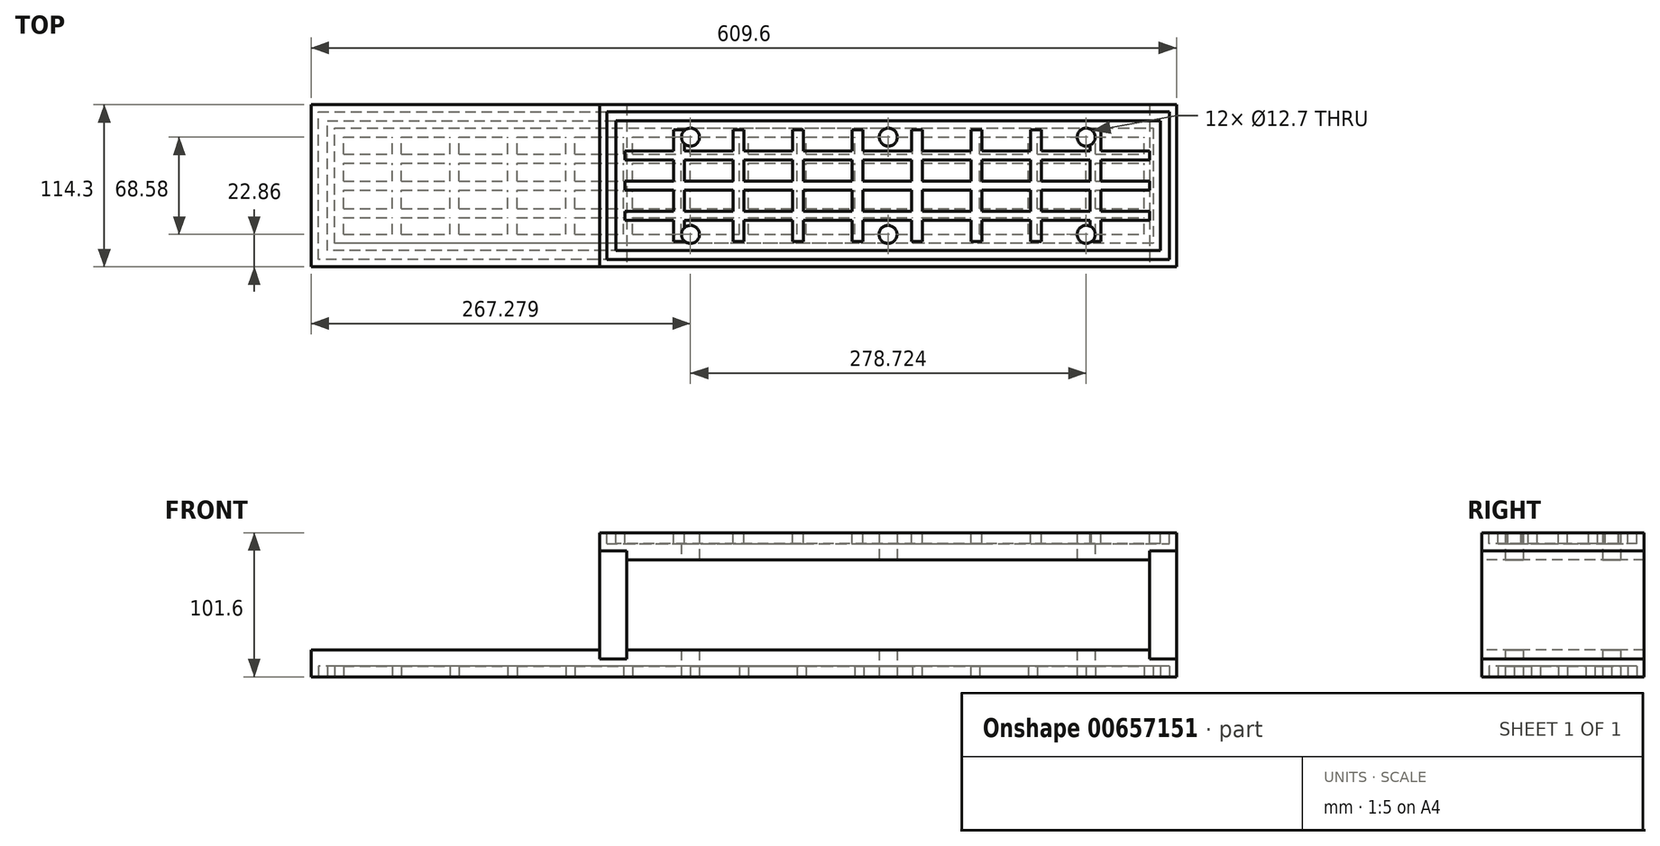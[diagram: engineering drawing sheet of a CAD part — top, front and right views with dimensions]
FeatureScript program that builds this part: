
annotation { "Feature Type Name" : "Feature", "Feature Type Description" : "" }
export const myFeature = defineFeature(function(context is Context, id is Id, definition is map)
    precondition{}
    {
        {
            var Q0;
            Q0=qCreatedBy(makeId("Front.planeOp"),FACE);
            var sketch = newSketch(context, id + "F0", { "sketchPlane" : qUnion([Q0])});
            skLineSegment(sketch, "E0.bottom", {"start": v(203.2, 50.8) * mm, "end": v(-203.2, 50.8) * mm});
            skLineSegment(sketch, "E0.top", {"start": v(203.2, -50.8) * mm, "end": v(-203.2, -50.8) * mm});
            skLineSegment(sketch, "E0.left", {"start": v(203.2, 50.8) * mm, "end": v(203.2, -50.8) * mm});
            skLineSegment(sketch, "E0.right", {"start": v(-203.2, 50.8) * mm, "end": v(-203.2, -38.1) * mm});
            skPoint(sketch, "E0.middle", {"position": v(0, 0) * mm});
            skLineSegment(sketch, "E1.0", {"start": v(184.15, 31.75) * mm, "end": v(-184.15, 31.75) * mm});
            skLineSegment(sketch, "E1.1", {"start": v(184.15, 31.75) * mm, "end": v(184.15, -31.75) * mm});
            skLineSegment(sketch, "E1.2", {"start": v(184.15, -31.75) * mm, "end": v(-184.15, -31.75) * mm});
            skLineSegment(sketch, "E1.3", {"start": v(-184.15, 31.75) * mm, "end": v(-184.15, -31.75) * mm});
            skLineSegment(sketch, "E2", {"start": v(-184.15, 31.75) * mm, "end": v(-184.15, 38.1) * mm});
            skLineSegment(sketch, "E3", {"start": v(-184.15, 38.1) * mm, "end": v(-203.2, 38.1) * mm});
            skLineSegment(sketch, "E4", {"start": v(-184.15, -31.75) * mm, "end": v(-184.15, -38.1) * mm});
            skLineSegment(sketch, "E5", {"start": v(-184.15, -38.1) * mm, "end": v(-203.2, -38.1) * mm});
            skLineSegment(sketch, "E6", {"start": v(184.15, -31.75) * mm, "end": v(184.15, -38.1) * mm});
            skLineSegment(sketch, "E7", {"start": v(184.15, -38.1) * mm, "end": v(203.2, -38.1) * mm});
            skLineSegment(sketch, "E8", {"start": v(184.15, 31.75) * mm, "end": v(184.15, 38.1) * mm});
            skLineSegment(sketch, "E9", {"start": v(184.15, 38.1) * mm, "end": v(203.2, 38.1) * mm});
            skLineSegment(sketch, "E10.bottom", {"start": v(-203.2, -50.8) * mm, "end": v(-406.4, -50.8) * mm});
            skLineSegment(sketch, "E10.top", {"start": v(-203.2, -31.75) * mm, "end": v(-406.4, -31.75) * mm});
            skLineSegment(sketch, "E10.left", {"start": v(-203.2, -38.1) * mm, "end": v(-203.2, -31.75) * mm});
            skLineSegment(sketch, "E10.right", {"start": v(-406.4, -50.8) * mm, "end": v(-406.4, -31.75) * mm});
            skSolve(sketch);
        }
        {
            var Q0;
            {var subQ2=sQuery(id+"F0.wireOp",EDGE,"E0.bottom");Q0=makeQuery(id+"F0.imprint","IMPRINT",FACE,{"disambiguationData":[TD([[makeQuery(id+"F0.imprint","IMPRINT",EDGE,{"derivedFrom":subQ2}),1.0]])]});}
            var Q1;
            {var subQ1=sQuery(id+"F0.wireOp",EDGE,"E0.top");Q1=makeQuery(id+"F0.imprint","IMPRINT",FACE,{"disambiguationData":[TD([[makeQuery(id+"F0.imprint","IMPRINT",EDGE,{"derivedFrom":subQ1}),-1.0]])]});}
            extrude(context, id + "F1", {"entities" : qUnion([Q0, Q1]), "oppositeDirection" : true, "depth" : 114.3 * mm, "offsetDistance" : 25.4 * mm});
        }
        {
            var Q0;
            Q0=makeQuery(id+"F0.imprint","IMPRINT",FACE,{"disambiguationData":[TD([[makeQuery(id+"F0.imprint","IMPRINT",EDGE,{"derivedFrom":sQuery(id+"F0.wireOp",EDGE,"E1.3")}),-1.0]])]});
            var Q1;
            Q1=makeQuery(id+"F0.imprint","IMPRINT",FACE,{"disambiguationData":[TD([[makeQuery(id+"F0.imprint","IMPRINT",EDGE,{"derivedFrom":sQuery(id+"F0.wireOp",EDGE,"E1.1")}),1.0]])]});
            extrude(context, id + "F2", {"entities" : qUnion([Q0, Q1]), "oppositeDirection" : true, "depth" : 114.3 * mm, "offsetDistance" : 25.4 * mm});
        }
        {
            var Q0;
            Q0=makeQuery(id+"F1.opExtrude","SWEPT_FACE",FACE,{"disambiguationData":[OSD([sQuery(id+"F0.wireOp",EDGE,"E0.top"),sQuery(id+"F0.wireOp",EDGE,"E10.bottom")])]});
            var sketch = newSketch(context, id + "F3", { "sketchPlane" : qUnion([Q0])});
            skLineSegment(sketch, "E11.0", {"start": v(198.12, -5.08) * mm, "end": v(-401.32, -5.08) * mm});
            skLineSegment(sketch, "E11.1", {"start": v(198.12, -109.22) * mm, "end": v(198.12, -5.08) * mm});
            skLineSegment(sketch, "E11.2", {"start": v(-401.32, -109.22) * mm, "end": v(198.12, -109.22) * mm});
            skLineSegment(sketch, "E11.3", {"start": v(-401.32, -5.08) * mm, "end": v(-401.32, -109.22) * mm});
            skLineSegment(sketch, "E12.0", {"start": v(191.77, -11.43) * mm, "end": v(-394.97, -11.43) * mm});
            skLineSegment(sketch, "E12.1", {"start": v(191.77, -102.87) * mm, "end": v(191.77, -11.43) * mm});
            skLineSegment(sketch, "E12.2", {"start": v(-394.97, -102.87) * mm, "end": v(191.77, -102.87) * mm});
            skLineSegment(sketch, "E12.3", {"start": v(-394.97, -11.43) * mm, "end": v(-394.97, -102.87) * mm});
            skLineSegment(sketch, "E13.bottom", {"start": v(-383.54, -22.86) * mm, "end": v(-349.23, -22.86) * mm});
            skLineSegment(sketch, "E13.top", {"start": v(-383.54, -34.8) * mm, "end": v(-349.23, -34.8) * mm});
            skLineSegment(sketch, "E13.left", {"start": v(-383.54, -22.86) * mm, "end": v(-383.54, -34.8) * mm});
            skLineSegment(sketch, "E13.right", {"start": v(-349.23, -22.86) * mm, "end": v(-349.23, -34.8) * mm});
            skLineSegment(sketch, "E14.bottom", {"start": v(-383.54, -41.15) * mm, "end": v(-349.23, -41.15) * mm});
            skLineSegment(sketch, "E14.top", {"start": v(-383.54, -53.99) * mm, "end": v(-349.23, -53.99) * mm});
            skLineSegment(sketch, "E14.left", {"start": v(-383.54, -41.15) * mm, "end": v(-383.54, -53.99) * mm});
            skLineSegment(sketch, "E14.right", {"start": v(-349.23, -41.15) * mm, "end": v(-349.23, -53.99) * mm});
            skLineSegment(sketch, "E15.bottom", {"start": v(-383.54, -79.53) * mm, "end": v(-349.23, -79.53) * mm});
            skLineSegment(sketch, "E15.top", {"start": v(-383.54, -91.44) * mm, "end": v(-349.23, -91.44) * mm});
            skLineSegment(sketch, "E15.left", {"start": v(-383.54, -79.53) * mm, "end": v(-383.54, -91.44) * mm});
            skLineSegment(sketch, "E15.right", {"start": v(-349.23, -79.53) * mm, "end": v(-349.23, -91.44) * mm});
            skLineSegment(sketch, "E16.1.0.0", {"start": v(-342.8, -34.8) * mm, "end": v(-308.5, -34.8) * mm});
            skLineSegment(sketch, "E16.1.0.1", {"start": v(-308.5, -79.53) * mm, "end": v(-308.5, -91.44) * mm});
            skLineSegment(sketch, "E16.1.0.2", {"start": v(-308.5, -41.15) * mm, "end": v(-308.5, -53.99) * mm});
            skLineSegment(sketch, "E16.1.0.3", {"start": v(-342.8, -22.86) * mm, "end": v(-308.5, -22.86) * mm});
            skLineSegment(sketch, "E16.1.0.4", {"start": v(-342.8, -41.15) * mm, "end": v(-308.5, -41.15) * mm});
            skLineSegment(sketch, "E16.1.0.5", {"start": v(-342.8, -22.86) * mm, "end": v(-342.8, -34.8) * mm});
            skLineSegment(sketch, "E16.1.0.6", {"start": v(-342.8, -91.44) * mm, "end": v(-308.5, -91.44) * mm});
            skLineSegment(sketch, "E16.1.0.7", {"start": v(-342.8, -79.53) * mm, "end": v(-342.8, -91.44) * mm});
            skLineSegment(sketch, "E16.1.0.8", {"start": v(-342.8, -79.53) * mm, "end": v(-308.5, -79.53) * mm});
            skLineSegment(sketch, "E16.1.0.9", {"start": v(-308.5, -22.86) * mm, "end": v(-308.5, -34.8) * mm});
            skLineSegment(sketch, "E16.1.0.10", {"start": v(-342.8, -41.15) * mm, "end": v(-342.8, -53.99) * mm});
            skLineSegment(sketch, "E16.1.0.11", {"start": v(-342.8, -53.99) * mm, "end": v(-308.5, -53.99) * mm});
            skLineSegment(sketch, "E16.2.0.0", {"start": v(-302.07, -34.8) * mm, "end": v(-267.76, -34.8) * mm});
            skLineSegment(sketch, "E16.2.0.1", {"start": v(-267.76, -79.53) * mm, "end": v(-267.76, -91.44) * mm});
            skLineSegment(sketch, "E16.2.0.2", {"start": v(-267.76, -41.15) * mm, "end": v(-267.76, -53.99) * mm});
            skLineSegment(sketch, "E16.2.0.3", {"start": v(-302.07, -22.86) * mm, "end": v(-267.76, -22.86) * mm});
            skLineSegment(sketch, "E16.2.0.4", {"start": v(-302.07, -41.15) * mm, "end": v(-267.76, -41.15) * mm});
            skLineSegment(sketch, "E16.2.0.5", {"start": v(-302.07, -22.86) * mm, "end": v(-302.07, -34.8) * mm});
            skLineSegment(sketch, "E16.2.0.6", {"start": v(-302.07, -91.44) * mm, "end": v(-267.76, -91.44) * mm});
            skLineSegment(sketch, "E16.2.0.7", {"start": v(-302.07, -79.53) * mm, "end": v(-302.07, -91.44) * mm});
            skLineSegment(sketch, "E16.2.0.8", {"start": v(-302.07, -79.53) * mm, "end": v(-267.76, -79.53) * mm});
            skLineSegment(sketch, "E16.2.0.9", {"start": v(-267.76, -22.86) * mm, "end": v(-267.76, -34.8) * mm});
            skLineSegment(sketch, "E16.2.0.10", {"start": v(-302.07, -41.15) * mm, "end": v(-302.07, -53.99) * mm});
            skLineSegment(sketch, "E16.2.0.11", {"start": v(-302.07, -53.99) * mm, "end": v(-267.76, -53.99) * mm});
            skLineSegment(sketch, "E16.3.0.0", {"start": v(-261.33, -34.8) * mm, "end": v(-227.03, -34.8) * mm});
            skLineSegment(sketch, "E16.3.0.1", {"start": v(-227.03, -79.53) * mm, "end": v(-227.03, -91.44) * mm});
            skLineSegment(sketch, "E16.3.0.2", {"start": v(-227.03, -41.15) * mm, "end": v(-227.03, -53.99) * mm});
            skLineSegment(sketch, "E16.3.0.3", {"start": v(-261.33, -22.86) * mm, "end": v(-227.03, -22.86) * mm});
            skLineSegment(sketch, "E16.3.0.4", {"start": v(-261.33, -41.15) * mm, "end": v(-227.03, -41.15) * mm});
            skLineSegment(sketch, "E16.3.0.5", {"start": v(-261.33, -22.86) * mm, "end": v(-261.33, -34.8) * mm});
            skLineSegment(sketch, "E16.3.0.6", {"start": v(-261.33, -91.44) * mm, "end": v(-227.03, -91.44) * mm});
            skLineSegment(sketch, "E16.3.0.7", {"start": v(-261.33, -79.53) * mm, "end": v(-261.33, -91.44) * mm});
            skLineSegment(sketch, "E16.3.0.8", {"start": v(-261.33, -79.53) * mm, "end": v(-227.03, -79.53) * mm});
            skLineSegment(sketch, "E16.3.0.9", {"start": v(-227.03, -22.86) * mm, "end": v(-227.03, -34.8) * mm});
            skLineSegment(sketch, "E16.3.0.10", {"start": v(-261.33, -41.15) * mm, "end": v(-261.33, -53.99) * mm});
            skLineSegment(sketch, "E16.3.0.11", {"start": v(-261.33, -53.99) * mm, "end": v(-227.03, -53.99) * mm});
            skLineSegment(sketch, "E16.4.0.0", {"start": v(-220.6, -34.8) * mm, "end": v(-186.29, -34.8) * mm});
            skLineSegment(sketch, "E16.4.0.1", {"start": v(-186.29, -79.53) * mm, "end": v(-186.29, -91.44) * mm});
            skLineSegment(sketch, "E16.4.0.2", {"start": v(-186.29, -41.15) * mm, "end": v(-186.29, -53.99) * mm});
            skLineSegment(sketch, "E16.4.0.3", {"start": v(-220.6, -22.86) * mm, "end": v(-186.29, -22.86) * mm});
            skLineSegment(sketch, "E16.4.0.4", {"start": v(-220.6, -41.15) * mm, "end": v(-186.29, -41.15) * mm});
            skLineSegment(sketch, "E16.4.0.5", {"start": v(-220.6, -22.86) * mm, "end": v(-220.6, -34.8) * mm});
            skLineSegment(sketch, "E16.4.0.6", {"start": v(-220.6, -91.44) * mm, "end": v(-186.29, -91.44) * mm});
            skLineSegment(sketch, "E16.4.0.7", {"start": v(-220.6, -79.53) * mm, "end": v(-220.6, -91.44) * mm});
            skLineSegment(sketch, "E16.4.0.8", {"start": v(-220.6, -79.53) * mm, "end": v(-186.29, -79.53) * mm});
            skLineSegment(sketch, "E16.4.0.9", {"start": v(-186.29, -22.86) * mm, "end": v(-186.29, -34.8) * mm});
            skLineSegment(sketch, "E16.4.0.10", {"start": v(-220.6, -41.15) * mm, "end": v(-220.6, -53.99) * mm});
            skLineSegment(sketch, "E16.4.0.11", {"start": v(-220.6, -53.99) * mm, "end": v(-186.29, -53.99) * mm});
            skLineSegment(sketch, "E16.5.0.0", {"start": v(-179.86, -34.8) * mm, "end": v(-145.55, -34.8) * mm});
            skLineSegment(sketch, "E16.5.0.1", {"start": v(-145.55, -79.53) * mm, "end": v(-145.55, -91.44) * mm});
            skLineSegment(sketch, "E16.5.0.2", {"start": v(-145.55, -41.15) * mm, "end": v(-145.55, -53.99) * mm});
            skLineSegment(sketch, "E16.5.0.3", {"start": v(-179.86, -22.86) * mm, "end": v(-145.55, -22.86) * mm});
            skLineSegment(sketch, "E16.5.0.4", {"start": v(-179.86, -41.15) * mm, "end": v(-145.55, -41.15) * mm});
            skLineSegment(sketch, "E16.5.0.5", {"start": v(-179.86, -22.86) * mm, "end": v(-179.86, -34.8) * mm});
            skLineSegment(sketch, "E16.5.0.6", {"start": v(-179.86, -91.44) * mm, "end": v(-145.55, -91.44) * mm});
            skLineSegment(sketch, "E16.5.0.7", {"start": v(-179.86, -79.53) * mm, "end": v(-179.86, -91.44) * mm});
            skLineSegment(sketch, "E16.5.0.8", {"start": v(-179.86, -79.53) * mm, "end": v(-145.55, -79.53) * mm});
            skLineSegment(sketch, "E16.5.0.9", {"start": v(-145.55, -22.86) * mm, "end": v(-145.55, -34.8) * mm});
            skLineSegment(sketch, "E16.5.0.10", {"start": v(-179.86, -41.15) * mm, "end": v(-179.86, -53.99) * mm});
            skLineSegment(sketch, "E16.5.0.11", {"start": v(-179.86, -53.99) * mm, "end": v(-145.55, -53.99) * mm});
            skLineSegment(sketch, "E16.6.0.0", {"start": v(-139.12, -34.8) * mm, "end": v(-104.82, -34.8) * mm});
            skLineSegment(sketch, "E16.6.0.1", {"start": v(-104.82, -79.53) * mm, "end": v(-104.82, -91.44) * mm});
            skLineSegment(sketch, "E16.6.0.2", {"start": v(-104.82, -41.15) * mm, "end": v(-104.82, -53.99) * mm});
            skLineSegment(sketch, "E16.6.0.3", {"start": v(-139.12, -22.86) * mm, "end": v(-104.82, -22.86) * mm});
            skLineSegment(sketch, "E16.6.0.4", {"start": v(-139.12, -41.15) * mm, "end": v(-104.82, -41.15) * mm});
            skLineSegment(sketch, "E16.6.0.5", {"start": v(-139.12, -22.86) * mm, "end": v(-139.12, -34.8) * mm});
            skLineSegment(sketch, "E16.6.0.6", {"start": v(-139.12, -91.44) * mm, "end": v(-104.82, -91.44) * mm});
            skLineSegment(sketch, "E16.6.0.7", {"start": v(-139.12, -79.53) * mm, "end": v(-139.12, -91.44) * mm});
            skLineSegment(sketch, "E16.6.0.8", {"start": v(-139.12, -79.53) * mm, "end": v(-104.82, -79.53) * mm});
            skLineSegment(sketch, "E16.6.0.9", {"start": v(-104.82, -22.86) * mm, "end": v(-104.82, -34.8) * mm});
            skLineSegment(sketch, "E16.6.0.10", {"start": v(-139.12, -41.15) * mm, "end": v(-139.12, -53.99) * mm});
            skLineSegment(sketch, "E16.6.0.11", {"start": v(-139.12, -53.99) * mm, "end": v(-104.82, -53.99) * mm});
            skLineSegment(sketch, "E16.7.0.0", {"start": v(-98.38, -34.8) * mm, "end": v(-64.08, -34.8) * mm});
            skLineSegment(sketch, "E16.7.0.1", {"start": v(-64.08, -79.53) * mm, "end": v(-64.08, -91.44) * mm});
            skLineSegment(sketch, "E16.7.0.2", {"start": v(-64.08, -41.15) * mm, "end": v(-64.08, -53.99) * mm});
            skLineSegment(sketch, "E16.7.0.3", {"start": v(-98.38, -22.86) * mm, "end": v(-64.08, -22.86) * mm});
            skLineSegment(sketch, "E16.7.0.4", {"start": v(-98.38, -41.15) * mm, "end": v(-64.08, -41.15) * mm});
            skLineSegment(sketch, "E16.7.0.5", {"start": v(-98.38, -22.86) * mm, "end": v(-98.38, -34.8) * mm});
            skLineSegment(sketch, "E16.7.0.6", {"start": v(-98.38, -91.44) * mm, "end": v(-64.08, -91.44) * mm});
            skLineSegment(sketch, "E16.7.0.7", {"start": v(-98.38, -79.53) * mm, "end": v(-98.38, -91.44) * mm});
            skLineSegment(sketch, "E16.7.0.8", {"start": v(-98.38, -79.53) * mm, "end": v(-64.08, -79.53) * mm});
            skLineSegment(sketch, "E16.7.0.9", {"start": v(-64.08, -22.86) * mm, "end": v(-64.08, -34.8) * mm});
            skLineSegment(sketch, "E16.7.0.10", {"start": v(-98.38, -41.15) * mm, "end": v(-98.38, -53.99) * mm});
            skLineSegment(sketch, "E16.7.0.11", {"start": v(-98.38, -53.99) * mm, "end": v(-64.08, -53.99) * mm});
            skLineSegment(sketch, "E16.8.0.0", {"start": v(-57.65, -34.8) * mm, "end": v(-23.34, -34.8) * mm});
            skLineSegment(sketch, "E16.8.0.1", {"start": v(-23.34, -79.53) * mm, "end": v(-23.34, -91.44) * mm});
            skLineSegment(sketch, "E16.8.0.2", {"start": v(-23.34, -41.15) * mm, "end": v(-23.34, -53.99) * mm});
            skLineSegment(sketch, "E16.8.0.3", {"start": v(-57.65, -22.86) * mm, "end": v(-23.34, -22.86) * mm});
            skLineSegment(sketch, "E16.8.0.4", {"start": v(-57.65, -41.15) * mm, "end": v(-23.34, -41.15) * mm});
            skLineSegment(sketch, "E16.8.0.5", {"start": v(-57.65, -22.86) * mm, "end": v(-57.65, -34.8) * mm});
            skLineSegment(sketch, "E16.8.0.6", {"start": v(-57.65, -91.44) * mm, "end": v(-23.34, -91.44) * mm});
            skLineSegment(sketch, "E16.8.0.7", {"start": v(-57.65, -79.53) * mm, "end": v(-57.65, -91.44) * mm});
            skLineSegment(sketch, "E16.8.0.8", {"start": v(-57.65, -79.53) * mm, "end": v(-23.34, -79.53) * mm});
            skLineSegment(sketch, "E16.8.0.9", {"start": v(-23.34, -22.86) * mm, "end": v(-23.34, -34.8) * mm});
            skLineSegment(sketch, "E16.8.0.10", {"start": v(-57.65, -41.15) * mm, "end": v(-57.65, -53.99) * mm});
            skLineSegment(sketch, "E16.8.0.11", {"start": v(-57.65, -53.99) * mm, "end": v(-23.34, -53.99) * mm});
            skLineSegment(sketch, "E16.9.0.0", {"start": v(-16.91, -34.8) * mm, "end": v(17.4, -34.8) * mm});
            skLineSegment(sketch, "E16.9.0.1", {"start": v(17.4, -79.53) * mm, "end": v(17.4, -91.44) * mm});
            skLineSegment(sketch, "E16.9.0.2", {"start": v(17.4, -41.15) * mm, "end": v(17.4, -53.99) * mm});
            skLineSegment(sketch, "E16.9.0.3", {"start": v(-16.91, -22.86) * mm, "end": v(17.4, -22.86) * mm});
            skLineSegment(sketch, "E16.9.0.4", {"start": v(-16.91, -41.15) * mm, "end": v(17.4, -41.15) * mm});
            skLineSegment(sketch, "E16.9.0.5", {"start": v(-16.91, -22.86) * mm, "end": v(-16.91, -34.8) * mm});
            skLineSegment(sketch, "E16.9.0.6", {"start": v(-16.91, -91.44) * mm, "end": v(17.4, -91.44) * mm});
            skLineSegment(sketch, "E16.9.0.7", {"start": v(-16.91, -79.53) * mm, "end": v(-16.91, -91.44) * mm});
            skLineSegment(sketch, "E16.9.0.8", {"start": v(-16.91, -79.53) * mm, "end": v(17.4, -79.53) * mm});
            skLineSegment(sketch, "E16.9.0.9", {"start": v(17.4, -22.86) * mm, "end": v(17.4, -34.8) * mm});
            skLineSegment(sketch, "E16.9.0.10", {"start": v(-16.91, -41.15) * mm, "end": v(-16.91, -53.99) * mm});
            skLineSegment(sketch, "E16.9.0.11", {"start": v(-16.91, -53.99) * mm, "end": v(17.4, -53.99) * mm});
            skLineSegment(sketch, "E16.10.0.0", {"start": v(23.83, -34.8) * mm, "end": v(58.13, -34.8) * mm});
            skLineSegment(sketch, "E16.10.0.1", {"start": v(58.13, -79.53) * mm, "end": v(58.13, -91.44) * mm});
            skLineSegment(sketch, "E16.10.0.2", {"start": v(58.13, -41.15) * mm, "end": v(58.13, -53.99) * mm});
            skLineSegment(sketch, "E16.10.0.3", {"start": v(23.83, -22.86) * mm, "end": v(58.13, -22.86) * mm});
            skLineSegment(sketch, "E16.10.0.4", {"start": v(23.83, -41.15) * mm, "end": v(58.13, -41.15) * mm});
            skLineSegment(sketch, "E16.10.0.5", {"start": v(23.83, -22.86) * mm, "end": v(23.83, -34.8) * mm});
            skLineSegment(sketch, "E16.10.0.6", {"start": v(23.83, -91.44) * mm, "end": v(58.13, -91.44) * mm});
            skLineSegment(sketch, "E16.10.0.7", {"start": v(23.83, -79.53) * mm, "end": v(23.83, -91.44) * mm});
            skLineSegment(sketch, "E16.10.0.8", {"start": v(23.83, -79.53) * mm, "end": v(58.13, -79.53) * mm});
            skLineSegment(sketch, "E16.10.0.9", {"start": v(58.13, -22.86) * mm, "end": v(58.13, -34.8) * mm});
            skLineSegment(sketch, "E16.10.0.10", {"start": v(23.83, -41.15) * mm, "end": v(23.83, -53.99) * mm});
            skLineSegment(sketch, "E16.10.0.11", {"start": v(23.83, -53.99) * mm, "end": v(58.13, -53.99) * mm});
            skLineSegment(sketch, "E16.11.0.0", {"start": v(64.56, -34.8) * mm, "end": v(98.87, -34.8) * mm});
            skLineSegment(sketch, "E16.11.0.1", {"start": v(98.87, -79.53) * mm, "end": v(98.87, -91.44) * mm});
            skLineSegment(sketch, "E16.11.0.2", {"start": v(98.87, -41.15) * mm, "end": v(98.87, -53.99) * mm});
            skLineSegment(sketch, "E16.11.0.3", {"start": v(64.56, -22.86) * mm, "end": v(98.87, -22.86) * mm});
            skLineSegment(sketch, "E16.11.0.4", {"start": v(64.56, -41.15) * mm, "end": v(98.87, -41.15) * mm});
            skLineSegment(sketch, "E16.11.0.5", {"start": v(64.56, -22.86) * mm, "end": v(64.56, -34.8) * mm});
            skLineSegment(sketch, "E16.11.0.6", {"start": v(64.56, -91.44) * mm, "end": v(98.87, -91.44) * mm});
            skLineSegment(sketch, "E16.11.0.7", {"start": v(64.56, -79.53) * mm, "end": v(64.56, -91.44) * mm});
            skLineSegment(sketch, "E16.11.0.8", {"start": v(64.56, -79.53) * mm, "end": v(98.87, -79.53) * mm});
            skLineSegment(sketch, "E16.11.0.9", {"start": v(98.87, -22.86) * mm, "end": v(98.87, -34.8) * mm});
            skLineSegment(sketch, "E16.11.0.10", {"start": v(64.56, -41.15) * mm, "end": v(64.56, -53.99) * mm});
            skLineSegment(sketch, "E16.11.0.11", {"start": v(64.56, -53.99) * mm, "end": v(98.87, -53.99) * mm});
            skLineSegment(sketch, "E16.12.0.0", {"start": v(105.3, -34.8) * mm, "end": v(139.6, -34.8) * mm});
            skLineSegment(sketch, "E16.12.0.1", {"start": v(139.6, -79.53) * mm, "end": v(139.6, -91.44) * mm});
            skLineSegment(sketch, "E16.12.0.2", {"start": v(139.6, -41.15) * mm, "end": v(139.6, -53.99) * mm});
            skLineSegment(sketch, "E16.12.0.3", {"start": v(105.3, -22.86) * mm, "end": v(139.6, -22.86) * mm});
            skLineSegment(sketch, "E16.12.0.4", {"start": v(105.3, -41.15) * mm, "end": v(139.6, -41.15) * mm});
            skLineSegment(sketch, "E16.12.0.5", {"start": v(105.3, -22.86) * mm, "end": v(105.3, -34.8) * mm});
            skLineSegment(sketch, "E16.12.0.6", {"start": v(105.3, -91.44) * mm, "end": v(139.6, -91.44) * mm});
            skLineSegment(sketch, "E16.12.0.7", {"start": v(105.3, -79.53) * mm, "end": v(105.3, -91.44) * mm});
            skLineSegment(sketch, "E16.12.0.8", {"start": v(105.3, -79.53) * mm, "end": v(139.6, -79.53) * mm});
            skLineSegment(sketch, "E16.12.0.9", {"start": v(139.6, -22.86) * mm, "end": v(139.6, -34.8) * mm});
            skLineSegment(sketch, "E16.12.0.10", {"start": v(105.3, -41.15) * mm, "end": v(105.3, -53.99) * mm});
            skLineSegment(sketch, "E16.12.0.11", {"start": v(105.3, -53.99) * mm, "end": v(139.6, -53.99) * mm});
            skLineSegment(sketch, "E16.13.0.0", {"start": v(146.03, -34.8) * mm, "end": v(180.34, -34.8) * mm});
            skLineSegment(sketch, "E16.13.0.1", {"start": v(180.34, -79.53) * mm, "end": v(180.34, -91.44) * mm});
            skLineSegment(sketch, "E16.13.0.2", {"start": v(180.34, -41.15) * mm, "end": v(180.34, -53.99) * mm});
            skLineSegment(sketch, "E16.13.0.3", {"start": v(146.03, -22.86) * mm, "end": v(180.34, -22.86) * mm});
            skLineSegment(sketch, "E16.13.0.4", {"start": v(146.03, -41.15) * mm, "end": v(180.34, -41.15) * mm});
            skLineSegment(sketch, "E16.13.0.5", {"start": v(146.03, -22.86) * mm, "end": v(146.03, -34.8) * mm});
            skLineSegment(sketch, "E16.13.0.6", {"start": v(146.03, -91.44) * mm, "end": v(180.34, -91.44) * mm});
            skLineSegment(sketch, "E16.13.0.7", {"start": v(146.03, -79.53) * mm, "end": v(146.03, -91.44) * mm});
            skLineSegment(sketch, "E16.13.0.8", {"start": v(146.03, -79.53) * mm, "end": v(180.34, -79.53) * mm});
            skLineSegment(sketch, "E16.13.0.9", {"start": v(180.34, -22.86) * mm, "end": v(180.34, -34.8) * mm});
            skLineSegment(sketch, "E16.13.0.10", {"start": v(146.03, -41.15) * mm, "end": v(146.03, -53.99) * mm});
            skLineSegment(sketch, "E16.13.0.11", {"start": v(146.03, -53.99) * mm, "end": v(180.34, -53.99) * mm});
            skLineSegment(sketch, "E16.direction1", {"start": v(-383.54, -91.44) * mm, "end": v(-342.8, -91.44) * mm, "construction": true});
            skLineSegment(sketch, "E17.bottom", {"start": v(-383.54, -60.34) * mm, "end": v(-349.23, -60.34) * mm});
            skLineSegment(sketch, "E17.top", {"start": v(-383.54, -73.18) * mm, "end": v(-349.23, -73.18) * mm});
            skLineSegment(sketch, "E17.left", {"start": v(-383.54, -60.34) * mm, "end": v(-383.54, -73.18) * mm});
            skLineSegment(sketch, "E17.right", {"start": v(-349.23, -60.34) * mm, "end": v(-349.23, -73.18) * mm});
            skLineSegment(sketch, "E18.1.0.0", {"start": v(-308.5, -60.34) * mm, "end": v(-308.5, -73.18) * mm});
            skLineSegment(sketch, "E18.1.0.1", {"start": v(-342.8, -60.34) * mm, "end": v(-308.5, -60.34) * mm});
            skLineSegment(sketch, "E18.1.0.2", {"start": v(-342.8, -73.18) * mm, "end": v(-308.5, -73.18) * mm});
            skLineSegment(sketch, "E18.1.0.3", {"start": v(-342.8, -60.34) * mm, "end": v(-342.8, -73.18) * mm});
            skLineSegment(sketch, "E18.2.0.0", {"start": v(-267.76, -60.34) * mm, "end": v(-267.76, -73.18) * mm});
            skLineSegment(sketch, "E18.2.0.1", {"start": v(-302.07, -60.34) * mm, "end": v(-267.76, -60.34) * mm});
            skLineSegment(sketch, "E18.2.0.2", {"start": v(-302.07, -73.18) * mm, "end": v(-267.76, -73.18) * mm});
            skLineSegment(sketch, "E18.2.0.3", {"start": v(-302.07, -60.34) * mm, "end": v(-302.07, -73.18) * mm});
            skLineSegment(sketch, "E18.3.0.0", {"start": v(-227.03, -60.34) * mm, "end": v(-227.03, -73.18) * mm});
            skLineSegment(sketch, "E18.3.0.1", {"start": v(-261.33, -60.34) * mm, "end": v(-227.03, -60.34) * mm});
            skLineSegment(sketch, "E18.3.0.2", {"start": v(-261.33, -73.18) * mm, "end": v(-227.03, -73.18) * mm});
            skLineSegment(sketch, "E18.3.0.3", {"start": v(-261.33, -60.34) * mm, "end": v(-261.33, -73.18) * mm});
            skLineSegment(sketch, "E18.4.0.0", {"start": v(-186.29, -60.34) * mm, "end": v(-186.29, -73.18) * mm});
            skLineSegment(sketch, "E18.4.0.1", {"start": v(-220.6, -60.34) * mm, "end": v(-186.29, -60.34) * mm});
            skLineSegment(sketch, "E18.4.0.2", {"start": v(-220.6, -73.18) * mm, "end": v(-186.29, -73.18) * mm});
            skLineSegment(sketch, "E18.4.0.3", {"start": v(-220.6, -60.34) * mm, "end": v(-220.6, -73.18) * mm});
            skLineSegment(sketch, "E18.5.0.0", {"start": v(-145.55, -60.34) * mm, "end": v(-145.55, -73.18) * mm});
            skLineSegment(sketch, "E18.5.0.1", {"start": v(-179.86, -60.34) * mm, "end": v(-145.55, -60.34) * mm});
            skLineSegment(sketch, "E18.5.0.2", {"start": v(-179.86, -73.18) * mm, "end": v(-145.55, -73.18) * mm});
            skLineSegment(sketch, "E18.5.0.3", {"start": v(-179.86, -60.34) * mm, "end": v(-179.86, -73.18) * mm});
            skLineSegment(sketch, "E18.6.0.0", {"start": v(-104.82, -60.34) * mm, "end": v(-104.82, -73.18) * mm});
            skLineSegment(sketch, "E18.6.0.1", {"start": v(-139.12, -60.34) * mm, "end": v(-104.82, -60.34) * mm});
            skLineSegment(sketch, "E18.6.0.2", {"start": v(-139.12, -73.18) * mm, "end": v(-104.82, -73.18) * mm});
            skLineSegment(sketch, "E18.6.0.3", {"start": v(-139.12, -60.34) * mm, "end": v(-139.12, -73.18) * mm});
            skLineSegment(sketch, "E18.7.0.0", {"start": v(-64.08, -60.34) * mm, "end": v(-64.08, -73.18) * mm});
            skLineSegment(sketch, "E18.7.0.1", {"start": v(-98.38, -60.34) * mm, "end": v(-64.08, -60.34) * mm});
            skLineSegment(sketch, "E18.7.0.2", {"start": v(-98.38, -73.18) * mm, "end": v(-64.08, -73.18) * mm});
            skLineSegment(sketch, "E18.7.0.3", {"start": v(-98.38, -60.34) * mm, "end": v(-98.38, -73.18) * mm});
            skLineSegment(sketch, "E18.8.0.0", {"start": v(-23.34, -60.34) * mm, "end": v(-23.34, -73.18) * mm});
            skLineSegment(sketch, "E18.8.0.1", {"start": v(-57.65, -60.34) * mm, "end": v(-23.34, -60.34) * mm});
            skLineSegment(sketch, "E18.8.0.2", {"start": v(-57.65, -73.18) * mm, "end": v(-23.34, -73.18) * mm});
            skLineSegment(sketch, "E18.8.0.3", {"start": v(-57.65, -60.34) * mm, "end": v(-57.65, -73.18) * mm});
            skLineSegment(sketch, "E18.9.0.0", {"start": v(17.4, -60.34) * mm, "end": v(17.4, -73.18) * mm});
            skLineSegment(sketch, "E18.9.0.1", {"start": v(-16.91, -60.34) * mm, "end": v(17.4, -60.34) * mm});
            skLineSegment(sketch, "E18.9.0.2", {"start": v(-16.91, -73.18) * mm, "end": v(17.4, -73.18) * mm});
            skLineSegment(sketch, "E18.9.0.3", {"start": v(-16.91, -60.34) * mm, "end": v(-16.91, -73.18) * mm});
            skLineSegment(sketch, "E18.10.0.0", {"start": v(58.13, -60.34) * mm, "end": v(58.13, -73.18) * mm});
            skLineSegment(sketch, "E18.10.0.1", {"start": v(23.83, -60.34) * mm, "end": v(58.13, -60.34) * mm});
            skLineSegment(sketch, "E18.10.0.2", {"start": v(23.83, -73.18) * mm, "end": v(58.13, -73.18) * mm});
            skLineSegment(sketch, "E18.10.0.3", {"start": v(23.83, -60.34) * mm, "end": v(23.83, -73.18) * mm});
            skLineSegment(sketch, "E18.11.0.0", {"start": v(98.87, -60.34) * mm, "end": v(98.87, -73.18) * mm});
            skLineSegment(sketch, "E18.11.0.1", {"start": v(64.56, -60.34) * mm, "end": v(98.87, -60.34) * mm});
            skLineSegment(sketch, "E18.11.0.2", {"start": v(64.56, -73.18) * mm, "end": v(98.87, -73.18) * mm});
            skLineSegment(sketch, "E18.11.0.3", {"start": v(64.56, -60.34) * mm, "end": v(64.56, -73.18) * mm});
            skLineSegment(sketch, "E18.12.0.0", {"start": v(139.6, -60.34) * mm, "end": v(139.6, -73.18) * mm});
            skLineSegment(sketch, "E18.12.0.1", {"start": v(105.3, -60.34) * mm, "end": v(139.6, -60.34) * mm});
            skLineSegment(sketch, "E18.12.0.2", {"start": v(105.3, -73.18) * mm, "end": v(139.6, -73.18) * mm});
            skLineSegment(sketch, "E18.12.0.3", {"start": v(105.3, -60.34) * mm, "end": v(105.3, -73.18) * mm});
            skLineSegment(sketch, "E18.13.0.0", {"start": v(180.34, -60.34) * mm, "end": v(180.34, -73.18) * mm});
            skLineSegment(sketch, "E18.13.0.1", {"start": v(146.03, -60.34) * mm, "end": v(180.34, -60.34) * mm});
            skLineSegment(sketch, "E18.13.0.2", {"start": v(146.03, -73.18) * mm, "end": v(180.34, -73.18) * mm});
            skLineSegment(sketch, "E18.13.0.3", {"start": v(146.03, -60.34) * mm, "end": v(146.03, -73.18) * mm});
            skLineSegment(sketch, "E18.direction1", {"start": v(-383.54, -73.18) * mm, "end": v(-342.8, -73.18) * mm, "construction": true});
            skLineSegment(sketch, "E19.0", {"start": v(186.7, -16.5) * mm, "end": v(-389.9, -16.51) * mm});
            skLineSegment(sketch, "E19.1", {"start": v(186.7, -97.79) * mm, "end": v(186.7, -16.5) * mm});
            skLineSegment(sketch, "E19.2", {"start": v(-389.9, -97.8) * mm, "end": v(186.7, -97.79) * mm});
            skLineSegment(sketch, "E19.3", {"start": v(-389.9, -16.51) * mm, "end": v(-389.9, -97.8) * mm});
            skPoint(sketch, "E20.centerSnap0", {"position": v(0.24, -22.86) * mm});
            skPoint(sketch, "E20.center.orphan", {"position": v(0, -22.86) * mm});
            skPoint(sketch, "E21.center.orphan", {"position": v(0.24, -91.44) * mm});
            skSolve(sketch);
        }
        {
            var Q0;
            Q0=makeQuery(id+"F3.imprint","IMPRINT",FACE,{"disambiguationData":[TD([[makeQuery(id+"F3.imprint","IMPRINT",EDGE,{"derivedFrom":sQuery(id+"F3.wireOp",EDGE,"E11.0")}),1.0]])]});
            var Q1;
            Q1=makeQuery(id+"F3.imprint","IMPRINT",FACE,{"disambiguationData":[TD([[makeQuery(id+"F3.imprint","IMPRINT",EDGE,{"derivedFrom":sQuery(id+"F3.wireOp",EDGE,"E13.bottom")}),1.0]])]});
            extrude(context, id + "F4", {"entities" : qUnion([Q0, Q1]), "operationType" : NewBodyOperationType.REMOVE, "oppositeDirection" : true, "depth" : 7.62 * mm, "offsetDistance" : 25.4 * mm});
        }
        {
            var Q0;
            Q0=makeQuery(id+"F3.imprint","IMPRINT",FACE,{"disambiguationData":[TD([[makeQuery(id+"F3.imprint","IMPRINT",EDGE,{"derivedFrom":sQuery(id+"F3.wireOp",EDGE,"E11.0")}),-1.0]])]});
            var sketch = newSketch(context, id + "F5", { "sketchPlane" : qUnion([Q0])});
            skCircle(sketch, "E22", {"center": v(-139.12, -22.86) * mm, "radius": 6.35 * mm});
            skCircle(sketch, "E23", {"center": v(-139.12, -91.44) * mm, "radius": 6.35 * mm});
            skCircle(sketch, "E24", {"center": v(139.6, -22.86) * mm, "radius": 6.35 * mm});
            skCircle(sketch, "E25", {"center": v(139.6, -91.44) * mm, "radius": 6.35 * mm});
            skCircle(sketch, "E26", {"center": v(0, -22.86) * mm, "radius": 6.35 * mm});
            skCircle(sketch, "E27", {"center": v(0.24, -91.44) * mm, "radius": 6.35 * mm});
            skSolve(sketch);
        }
        {
            var Q0;
            Q0=makeQuery(id+"F5.imprint","IMPRINT",FACE,{"disambiguationData":[TD([[makeQuery(id+"F5.imprint","IMPRINT",EDGE,{"derivedFrom":sQuery(id+"F5.wireOp",EDGE,"E25")}),1.0]])]});
            var Q1;
            Q1=makeQuery(id+"F5.imprint","IMPRINT",FACE,{"disambiguationData":[TD([[makeQuery(id+"F5.imprint","IMPRINT",EDGE,{"derivedFrom":sQuery(id+"F5.wireOp",EDGE,"E24")}),1.0]])]});
            var Q2;
            Q2=makeQuery(id+"F5.imprint","IMPRINT",FACE,{"disambiguationData":[TD([[makeQuery(id+"F5.imprint","IMPRINT",EDGE,{"derivedFrom":sQuery(id+"F5.wireOp",EDGE,"E26")}),1.0]])]});
            var Q3;
            Q3=makeQuery(id+"F5.imprint","IMPRINT",FACE,{"disambiguationData":[TD([[makeQuery(id+"F5.imprint","IMPRINT",EDGE,{"derivedFrom":sQuery(id+"F5.wireOp",EDGE,"E27")}),1.0]])]});
            var Q4;
            Q4=makeQuery(id+"F5.imprint","IMPRINT",FACE,{"disambiguationData":[TD([[makeQuery(id+"F5.imprint","IMPRINT",EDGE,{"derivedFrom":sQuery(id+"F5.wireOp",EDGE,"E22")}),1.0]])]});
            var Q5;
            Q5=makeQuery(id+"F5.imprint","IMPRINT",FACE,{"disambiguationData":[TD([[makeQuery(id+"F5.imprint","IMPRINT",EDGE,{"derivedFrom":sQuery(id+"F5.wireOp",EDGE,"E23")}),1.0]])]});
            extrude(context, id + "F6", {"entities" : qUnion([Q0, Q1, Q2, Q3, Q4, Q5]), "operationType" : NewBodyOperationType.REMOVE, "endBound" : BoundingType.THROUGH_ALL, "oppositeDirection" : true, "depth" : 25.4 * mm, "offsetDistance" : 25.4 * mm});
        }
        {
            var Q0;
            Q0=makeQuery(id+"F1.opExtrude","SWEPT_FACE",FACE,{"disambiguationData":[OSD([sQuery(id+"F0.wireOp",EDGE,"E0.bottom")])]});
            var sketch = newSketch(context, id + "F7", { "sketchPlane" : qUnion([Q0])});
            skLineSegment(sketch, "E28.0", {"start": v(-198.12, 5.08) * mm, "end": v(198.12, 5.08) * mm});
            skLineSegment(sketch, "E28.1", {"start": v(-198.12, 109.22) * mm, "end": v(-198.12, 5.08) * mm});
            skLineSegment(sketch, "E28.2", {"start": v(198.12, 109.22) * mm, "end": v(-198.12, 109.22) * mm});
            skLineSegment(sketch, "E28.3", {"start": v(198.12, 5.08) * mm, "end": v(198.12, 109.22) * mm});
            skLineSegment(sketch, "E29.0", {"start": v(191.77, 102.87) * mm, "end": v(-191.77, 102.87) * mm});
            skLineSegment(sketch, "E29.1", {"start": v(191.77, 11.43) * mm, "end": v(191.77, 102.87) * mm});
            skLineSegment(sketch, "E29.2", {"start": v(-191.77, 11.43) * mm, "end": v(191.77, 11.43) * mm});
            skLineSegment(sketch, "E29.3", {"start": v(-191.77, 102.87) * mm, "end": v(-191.77, 11.43) * mm});
            skLineSegment(sketch, "E30.bottom", {"start": v(-185.42, 96.52) * mm, "end": v(-150.88, 96.52) * mm});
            skLineSegment(sketch, "E30.top", {"start": v(-185.42, 81.6) * mm, "end": v(-150.88, 81.6) * mm});
            skLineSegment(sketch, "E30.left", {"start": v(-185.42, 96.52) * mm, "end": v(-185.42, 81.6) * mm});
            skLineSegment(sketch, "E30.right", {"start": v(-150.88, 96.52) * mm, "end": v(-150.88, 81.6) * mm});
            skLineSegment(sketch, "E31.bottom", {"start": v(-185.42, 17.78) * mm, "end": v(-150.88, 17.78) * mm});
            skLineSegment(sketch, "E31.top", {"start": v(-185.42, 32.7) * mm, "end": v(-150.88, 32.7) * mm});
            skLineSegment(sketch, "E31.left", {"start": v(-185.42, 17.78) * mm, "end": v(-185.42, 32.7) * mm});
            skLineSegment(sketch, "E31.right", {"start": v(-150.88, 17.78) * mm, "end": v(-150.88, 32.7) * mm});
            skLineSegment(sketch, "E32.bottom", {"start": v(-185.42, 39.05) * mm, "end": v(-150.88, 39.05) * mm});
            skLineSegment(sketch, "E32.top", {"start": v(-185.42, 53.98) * mm, "end": v(-150.88, 53.98) * mm});
            skLineSegment(sketch, "E32.left", {"start": v(-185.42, 39.05) * mm, "end": v(-185.42, 53.98) * mm});
            skLineSegment(sketch, "E32.right", {"start": v(-150.88, 39.05) * mm, "end": v(-150.88, 53.98) * mm});
            skLineSegment(sketch, "E33.bottom", {"start": v(-185.42, 60.33) * mm, "end": v(-150.88, 60.33) * mm});
            skLineSegment(sketch, "E33.top", {"start": v(-185.42, 75.25) * mm, "end": v(-150.88, 75.25) * mm});
            skLineSegment(sketch, "E33.left", {"start": v(-185.42, 60.33) * mm, "end": v(-185.42, 75.25) * mm});
            skLineSegment(sketch, "E33.right", {"start": v(-150.88, 60.33) * mm, "end": v(-150.88, 75.25) * mm});
            skLineSegment(sketch, "E34.1.0.0", {"start": v(-143.51, 75.25) * mm, "end": v(-108.97, 75.25) * mm});
            skLineSegment(sketch, "E34.1.0.1", {"start": v(-108.97, 60.33) * mm, "end": v(-108.97, 75.25) * mm});
            skLineSegment(sketch, "E34.1.0.2", {"start": v(-143.51, 53.98) * mm, "end": v(-108.97, 53.98) * mm});
            skLineSegment(sketch, "E34.1.0.3", {"start": v(-108.97, 96.52) * mm, "end": v(-108.97, 81.6) * mm});
            skLineSegment(sketch, "E34.1.0.4", {"start": v(-143.51, 17.78) * mm, "end": v(-108.97, 17.78) * mm});
            skLineSegment(sketch, "E34.1.0.5", {"start": v(-143.51, 96.52) * mm, "end": v(-143.51, 81.6) * mm});
            skLineSegment(sketch, "E34.1.0.6", {"start": v(-108.97, 39.05) * mm, "end": v(-108.97, 53.98) * mm});
            skLineSegment(sketch, "E34.1.0.7", {"start": v(-143.51, 60.33) * mm, "end": v(-108.97, 60.33) * mm});
            skLineSegment(sketch, "E34.1.0.8", {"start": v(-143.51, 96.52) * mm, "end": v(-108.97, 96.52) * mm});
            skLineSegment(sketch, "E34.1.0.9", {"start": v(-143.51, 32.7) * mm, "end": v(-108.97, 32.7) * mm});
            skLineSegment(sketch, "E34.1.0.10", {"start": v(-143.51, 81.6) * mm, "end": v(-108.97, 81.6) * mm});
            skLineSegment(sketch, "E34.1.0.11", {"start": v(-143.51, 39.05) * mm, "end": v(-143.51, 53.98) * mm});
            skLineSegment(sketch, "E34.1.0.12", {"start": v(-143.51, 60.33) * mm, "end": v(-143.51, 75.25) * mm});
            skLineSegment(sketch, "E34.1.0.13", {"start": v(-143.51, 39.05) * mm, "end": v(-108.97, 39.05) * mm});
            skLineSegment(sketch, "E34.1.0.14", {"start": v(-108.97, 17.78) * mm, "end": v(-108.97, 32.7) * mm});
            skLineSegment(sketch, "E34.1.0.15", {"start": v(-143.51, 17.78) * mm, "end": v(-143.51, 32.7) * mm});
            skLineSegment(sketch, "E34.2.0.0", {"start": v(-101.6, 75.25) * mm, "end": v(-67.06, 75.25) * mm});
            skLineSegment(sketch, "E34.2.0.1", {"start": v(-67.06, 60.33) * mm, "end": v(-67.06, 75.25) * mm});
            skLineSegment(sketch, "E34.2.0.2", {"start": v(-101.6, 53.98) * mm, "end": v(-67.06, 53.98) * mm});
            skLineSegment(sketch, "E34.2.0.3", {"start": v(-67.06, 96.52) * mm, "end": v(-67.06, 81.6) * mm});
            skLineSegment(sketch, "E34.2.0.4", {"start": v(-101.6, 17.78) * mm, "end": v(-67.06, 17.78) * mm});
            skLineSegment(sketch, "E34.2.0.5", {"start": v(-101.6, 96.52) * mm, "end": v(-101.6, 81.6) * mm});
            skLineSegment(sketch, "E34.2.0.6", {"start": v(-67.06, 39.05) * mm, "end": v(-67.06, 53.98) * mm});
            skLineSegment(sketch, "E34.2.0.7", {"start": v(-101.6, 60.33) * mm, "end": v(-67.06, 60.33) * mm});
            skLineSegment(sketch, "E34.2.0.8", {"start": v(-101.6, 96.52) * mm, "end": v(-67.06, 96.52) * mm});
            skLineSegment(sketch, "E34.2.0.9", {"start": v(-101.6, 32.7) * mm, "end": v(-67.06, 32.7) * mm});
            skLineSegment(sketch, "E34.2.0.10", {"start": v(-101.6, 81.6) * mm, "end": v(-67.06, 81.6) * mm});
            skLineSegment(sketch, "E34.2.0.11", {"start": v(-101.6, 39.05) * mm, "end": v(-101.6, 53.98) * mm});
            skLineSegment(sketch, "E34.2.0.12", {"start": v(-101.6, 60.33) * mm, "end": v(-101.6, 75.25) * mm});
            skLineSegment(sketch, "E34.2.0.13", {"start": v(-101.6, 39.05) * mm, "end": v(-67.06, 39.05) * mm});
            skLineSegment(sketch, "E34.2.0.14", {"start": v(-67.06, 17.78) * mm, "end": v(-67.06, 32.7) * mm});
            skLineSegment(sketch, "E34.2.0.15", {"start": v(-101.6, 17.78) * mm, "end": v(-101.6, 32.7) * mm});
            skLineSegment(sketch, "E34.3.0.0", {"start": v(-59.7, 75.25) * mm, "end": v(-25.15, 75.25) * mm});
            skLineSegment(sketch, "E34.3.0.1", {"start": v(-25.15, 60.33) * mm, "end": v(-25.15, 75.25) * mm});
            skLineSegment(sketch, "E34.3.0.2", {"start": v(-59.7, 53.98) * mm, "end": v(-25.15, 53.98) * mm});
            skLineSegment(sketch, "E34.3.0.3", {"start": v(-25.15, 96.52) * mm, "end": v(-25.15, 81.6) * mm});
            skLineSegment(sketch, "E34.3.0.4", {"start": v(-59.7, 17.78) * mm, "end": v(-25.15, 17.78) * mm});
            skLineSegment(sketch, "E34.3.0.5", {"start": v(-59.7, 96.52) * mm, "end": v(-59.7, 81.6) * mm});
            skLineSegment(sketch, "E34.3.0.6", {"start": v(-25.15, 39.05) * mm, "end": v(-25.15, 53.98) * mm});
            skLineSegment(sketch, "E34.3.0.7", {"start": v(-59.7, 60.33) * mm, "end": v(-25.15, 60.33) * mm});
            skLineSegment(sketch, "E34.3.0.8", {"start": v(-59.7, 96.52) * mm, "end": v(-25.15, 96.52) * mm});
            skLineSegment(sketch, "E34.3.0.9", {"start": v(-59.7, 32.7) * mm, "end": v(-25.15, 32.7) * mm});
            skLineSegment(sketch, "E34.3.0.10", {"start": v(-59.7, 81.6) * mm, "end": v(-25.15, 81.6) * mm});
            skLineSegment(sketch, "E34.3.0.11", {"start": v(-59.7, 39.05) * mm, "end": v(-59.7, 53.98) * mm});
            skLineSegment(sketch, "E34.3.0.12", {"start": v(-59.7, 60.33) * mm, "end": v(-59.7, 75.25) * mm});
            skLineSegment(sketch, "E34.3.0.13", {"start": v(-59.7, 39.05) * mm, "end": v(-25.15, 39.05) * mm});
            skLineSegment(sketch, "E34.3.0.14", {"start": v(-25.15, 17.78) * mm, "end": v(-25.15, 32.7) * mm});
            skLineSegment(sketch, "E34.3.0.15", {"start": v(-59.7, 17.78) * mm, "end": v(-59.7, 32.7) * mm});
            skLineSegment(sketch, "E34.4.0.0", {"start": v(-17.78, 75.25) * mm, "end": v(16.76, 75.25) * mm});
            skLineSegment(sketch, "E34.4.0.1", {"start": v(16.76, 60.33) * mm, "end": v(16.76, 75.25) * mm});
            skLineSegment(sketch, "E34.4.0.2", {"start": v(-17.78, 53.98) * mm, "end": v(16.76, 53.98) * mm});
            skLineSegment(sketch, "E34.4.0.3", {"start": v(16.76, 96.52) * mm, "end": v(16.76, 81.6) * mm});
            skLineSegment(sketch, "E34.4.0.4", {"start": v(-17.78, 17.78) * mm, "end": v(16.76, 17.78) * mm});
            skLineSegment(sketch, "E34.4.0.5", {"start": v(-17.78, 96.52) * mm, "end": v(-17.78, 81.6) * mm});
            skLineSegment(sketch, "E34.4.0.6", {"start": v(16.76, 39.05) * mm, "end": v(16.76, 53.98) * mm});
            skLineSegment(sketch, "E34.4.0.7", {"start": v(-17.78, 60.33) * mm, "end": v(16.76, 60.33) * mm});
            skLineSegment(sketch, "E34.4.0.8", {"start": v(-17.78, 96.52) * mm, "end": v(16.76, 96.52) * mm});
            skLineSegment(sketch, "E34.4.0.9", {"start": v(-17.78, 32.7) * mm, "end": v(16.76, 32.7) * mm});
            skLineSegment(sketch, "E34.4.0.10", {"start": v(-17.78, 81.6) * mm, "end": v(16.76, 81.6) * mm});
            skLineSegment(sketch, "E34.4.0.11", {"start": v(-17.78, 39.05) * mm, "end": v(-17.78, 53.98) * mm});
            skLineSegment(sketch, "E34.4.0.12", {"start": v(-17.78, 60.33) * mm, "end": v(-17.78, 75.25) * mm});
            skLineSegment(sketch, "E34.4.0.13", {"start": v(-17.78, 39.05) * mm, "end": v(16.76, 39.05) * mm});
            skLineSegment(sketch, "E34.4.0.14", {"start": v(16.76, 17.78) * mm, "end": v(16.76, 32.7) * mm});
            skLineSegment(sketch, "E34.4.0.15", {"start": v(-17.78, 17.78) * mm, "end": v(-17.78, 32.7) * mm});
            skLineSegment(sketch, "E34.5.0.0", {"start": v(24.13, 75.25) * mm, "end": v(58.67, 75.25) * mm});
            skLineSegment(sketch, "E34.5.0.1", {"start": v(58.67, 60.33) * mm, "end": v(58.67, 75.25) * mm});
            skLineSegment(sketch, "E34.5.0.2", {"start": v(24.13, 53.98) * mm, "end": v(58.67, 53.98) * mm});
            skLineSegment(sketch, "E34.5.0.3", {"start": v(58.67, 96.52) * mm, "end": v(58.67, 81.6) * mm});
            skLineSegment(sketch, "E34.5.0.4", {"start": v(24.13, 17.78) * mm, "end": v(58.67, 17.78) * mm});
            skLineSegment(sketch, "E34.5.0.5", {"start": v(24.13, 96.52) * mm, "end": v(24.13, 81.6) * mm});
            skLineSegment(sketch, "E34.5.0.6", {"start": v(58.67, 39.05) * mm, "end": v(58.67, 53.98) * mm});
            skLineSegment(sketch, "E34.5.0.7", {"start": v(24.13, 60.33) * mm, "end": v(58.67, 60.33) * mm});
            skLineSegment(sketch, "E34.5.0.8", {"start": v(24.13, 96.52) * mm, "end": v(58.67, 96.52) * mm});
            skLineSegment(sketch, "E34.5.0.9", {"start": v(24.13, 32.7) * mm, "end": v(58.67, 32.7) * mm});
            skLineSegment(sketch, "E34.5.0.10", {"start": v(24.13, 81.6) * mm, "end": v(58.67, 81.6) * mm});
            skLineSegment(sketch, "E34.5.0.11", {"start": v(24.13, 39.05) * mm, "end": v(24.13, 53.98) * mm});
            skLineSegment(sketch, "E34.5.0.12", {"start": v(24.13, 60.33) * mm, "end": v(24.13, 75.25) * mm});
            skLineSegment(sketch, "E34.5.0.13", {"start": v(24.13, 39.05) * mm, "end": v(58.67, 39.05) * mm});
            skLineSegment(sketch, "E34.5.0.14", {"start": v(58.67, 17.78) * mm, "end": v(58.67, 32.7) * mm});
            skLineSegment(sketch, "E34.5.0.15", {"start": v(24.13, 17.78) * mm, "end": v(24.13, 32.7) * mm});
            skLineSegment(sketch, "E34.6.0.0", {"start": v(66.04, 75.25) * mm, "end": v(100.58, 75.25) * mm});
            skLineSegment(sketch, "E34.6.0.1", {"start": v(100.58, 60.33) * mm, "end": v(100.58, 75.25) * mm});
            skLineSegment(sketch, "E34.6.0.2", {"start": v(66.04, 53.98) * mm, "end": v(100.58, 53.98) * mm});
            skLineSegment(sketch, "E34.6.0.3", {"start": v(100.58, 96.52) * mm, "end": v(100.58, 81.6) * mm});
            skLineSegment(sketch, "E34.6.0.4", {"start": v(66.04, 17.78) * mm, "end": v(100.58, 17.78) * mm});
            skLineSegment(sketch, "E34.6.0.5", {"start": v(66.04, 96.52) * mm, "end": v(66.04, 81.6) * mm});
            skLineSegment(sketch, "E34.6.0.6", {"start": v(100.58, 39.05) * mm, "end": v(100.58, 53.98) * mm});
            skLineSegment(sketch, "E34.6.0.7", {"start": v(66.04, 60.33) * mm, "end": v(100.58, 60.33) * mm});
            skLineSegment(sketch, "E34.6.0.8", {"start": v(66.04, 96.52) * mm, "end": v(100.58, 96.52) * mm});
            skLineSegment(sketch, "E34.6.0.9", {"start": v(66.04, 32.7) * mm, "end": v(100.58, 32.7) * mm});
            skLineSegment(sketch, "E34.6.0.10", {"start": v(66.04, 81.6) * mm, "end": v(100.58, 81.6) * mm});
            skLineSegment(sketch, "E34.6.0.11", {"start": v(66.04, 39.05) * mm, "end": v(66.04, 53.98) * mm});
            skLineSegment(sketch, "E34.6.0.12", {"start": v(66.04, 60.33) * mm, "end": v(66.04, 75.25) * mm});
            skLineSegment(sketch, "E34.6.0.13", {"start": v(66.04, 39.05) * mm, "end": v(100.58, 39.05) * mm});
            skLineSegment(sketch, "E34.6.0.14", {"start": v(100.58, 17.78) * mm, "end": v(100.58, 32.7) * mm});
            skLineSegment(sketch, "E34.6.0.15", {"start": v(66.04, 17.78) * mm, "end": v(66.04, 32.7) * mm});
            skLineSegment(sketch, "E34.direction1", {"start": v(-185.42, 17.78) * mm, "end": v(-143.51, 17.78) * mm, "construction": true});
            skLineSegment(sketch, "E35.0.7.0", {"start": v(107.95, 75.25) * mm, "end": v(142.5, 75.25) * mm});
            skLineSegment(sketch, "E35.3.7.0", {"start": v(142.5, 60.33) * mm, "end": v(142.5, 75.25) * mm});
            skLineSegment(sketch, "E35.6.7.0", {"start": v(107.95, 53.98) * mm, "end": v(142.5, 53.98) * mm});
            skLineSegment(sketch, "E35.9.7.0", {"start": v(142.5, 96.52) * mm, "end": v(142.5, 81.6) * mm});
            skLineSegment(sketch, "E35.12.7.0", {"start": v(107.95, 17.78) * mm, "end": v(142.5, 17.78) * mm});
            skLineSegment(sketch, "E35.15.7.0", {"start": v(107.95, 96.52) * mm, "end": v(107.95, 81.6) * mm});
            skLineSegment(sketch, "E35.18.7.0", {"start": v(142.5, 39.05) * mm, "end": v(142.5, 53.98) * mm});
            skLineSegment(sketch, "E35.21.7.0", {"start": v(107.95, 60.33) * mm, "end": v(142.5, 60.33) * mm});
            skLineSegment(sketch, "E35.24.7.0", {"start": v(107.95, 96.52) * mm, "end": v(142.5, 96.52) * mm});
            skLineSegment(sketch, "E35.27.7.0", {"start": v(107.95, 32.7) * mm, "end": v(142.5, 32.7) * mm});
            skLineSegment(sketch, "E35.30.7.0", {"start": v(107.95, 81.6) * mm, "end": v(142.5, 81.6) * mm});
            skLineSegment(sketch, "E35.33.7.0", {"start": v(107.95, 39.05) * mm, "end": v(107.95, 53.98) * mm});
            skLineSegment(sketch, "E35.36.7.0", {"start": v(107.95, 60.33) * mm, "end": v(107.95, 75.25) * mm});
            skLineSegment(sketch, "E35.39.7.0", {"start": v(107.95, 39.05) * mm, "end": v(142.5, 39.05) * mm});
            skLineSegment(sketch, "E35.42.7.0", {"start": v(142.5, 17.78) * mm, "end": v(142.5, 32.7) * mm});
            skLineSegment(sketch, "E35.45.7.0", {"start": v(107.95, 17.78) * mm, "end": v(107.95, 32.7) * mm});
            skLineSegment(sketch, "E35.0.8.0", {"start": v(149.86, 75.25) * mm, "end": v(184.4, 75.25) * mm});
            skLineSegment(sketch, "E35.3.8.0", {"start": v(184.4, 60.33) * mm, "end": v(184.4, 75.25) * mm});
            skLineSegment(sketch, "E35.6.8.0", {"start": v(149.86, 53.98) * mm, "end": v(184.4, 53.98) * mm});
            skLineSegment(sketch, "E35.9.8.0", {"start": v(184.4, 96.52) * mm, "end": v(184.4, 81.6) * mm});
            skLineSegment(sketch, "E35.12.8.0", {"start": v(149.86, 17.78) * mm, "end": v(184.4, 17.78) * mm});
            skLineSegment(sketch, "E35.15.8.0", {"start": v(149.86, 96.52) * mm, "end": v(149.86, 81.6) * mm});
            skLineSegment(sketch, "E35.18.8.0", {"start": v(184.4, 39.05) * mm, "end": v(184.4, 53.98) * mm});
            skLineSegment(sketch, "E35.21.8.0", {"start": v(149.86, 60.33) * mm, "end": v(184.4, 60.33) * mm});
            skLineSegment(sketch, "E35.24.8.0", {"start": v(149.86, 96.52) * mm, "end": v(184.4, 96.52) * mm});
            skLineSegment(sketch, "E35.27.8.0", {"start": v(149.86, 32.7) * mm, "end": v(184.4, 32.7) * mm});
            skLineSegment(sketch, "E35.30.8.0", {"start": v(149.86, 81.6) * mm, "end": v(184.4, 81.6) * mm});
            skLineSegment(sketch, "E35.33.8.0", {"start": v(149.86, 39.05) * mm, "end": v(149.86, 53.98) * mm});
            skLineSegment(sketch, "E35.36.8.0", {"start": v(149.86, 60.33) * mm, "end": v(149.86, 75.25) * mm});
            skLineSegment(sketch, "E35.39.8.0", {"start": v(149.86, 39.05) * mm, "end": v(184.4, 39.05) * mm});
            skLineSegment(sketch, "E35.42.8.0", {"start": v(184.4, 17.78) * mm, "end": v(184.4, 32.7) * mm});
            skLineSegment(sketch, "E35.45.8.0", {"start": v(149.86, 17.78) * mm, "end": v(149.86, 32.7) * mm});
            skLineSegment(sketch, "E36.bottom", {"start": v(-185.42, 96.52) * mm, "end": v(184.4, 96.52) * mm});
            skLineSegment(sketch, "E36.top", {"start": v(-185.42, 17.78) * mm, "end": v(184.4, 17.78) * mm});
            skLineSegment(sketch, "E36.left", {"start": v(-185.42, 96.52) * mm, "end": v(-185.42, 17.78) * mm});
            skLineSegment(sketch, "E36.right", {"start": v(184.4, 96.52) * mm, "end": v(184.4, 17.78) * mm});
            skSolve(sketch);
        }
        {
            var Q0;
            Q0=makeQuery(id+"F7.imprint","IMPRINT",FACE,{"disambiguationData":[TD([[makeQuery(id+"F7.imprint","IMPRINT",EDGE,{"derivedFrom":sQuery(id+"F7.wireOp",EDGE,"E28.0")}),1.0]])]});
            var Q1;
            {var subQ31=sQuery(id+"F7.wireOp",EDGE,"E30.top");Q1=makeQuery(id+"F7.imprint","IMPRINT",FACE,{"disambiguationData":[TD([[makeQuery(id+"F7.imprint","IMPRINT",EDGE,{"derivedFrom":subQ31}),-1.0]])]});}
            extrude(context, id + "F8", {"entities" : qUnion([Q0, Q1]), "operationType" : NewBodyOperationType.REMOVE, "oppositeDirection" : true, "depth" : 7.62 * mm, "offsetDistance" : 25.4 * mm});
        }
    });
